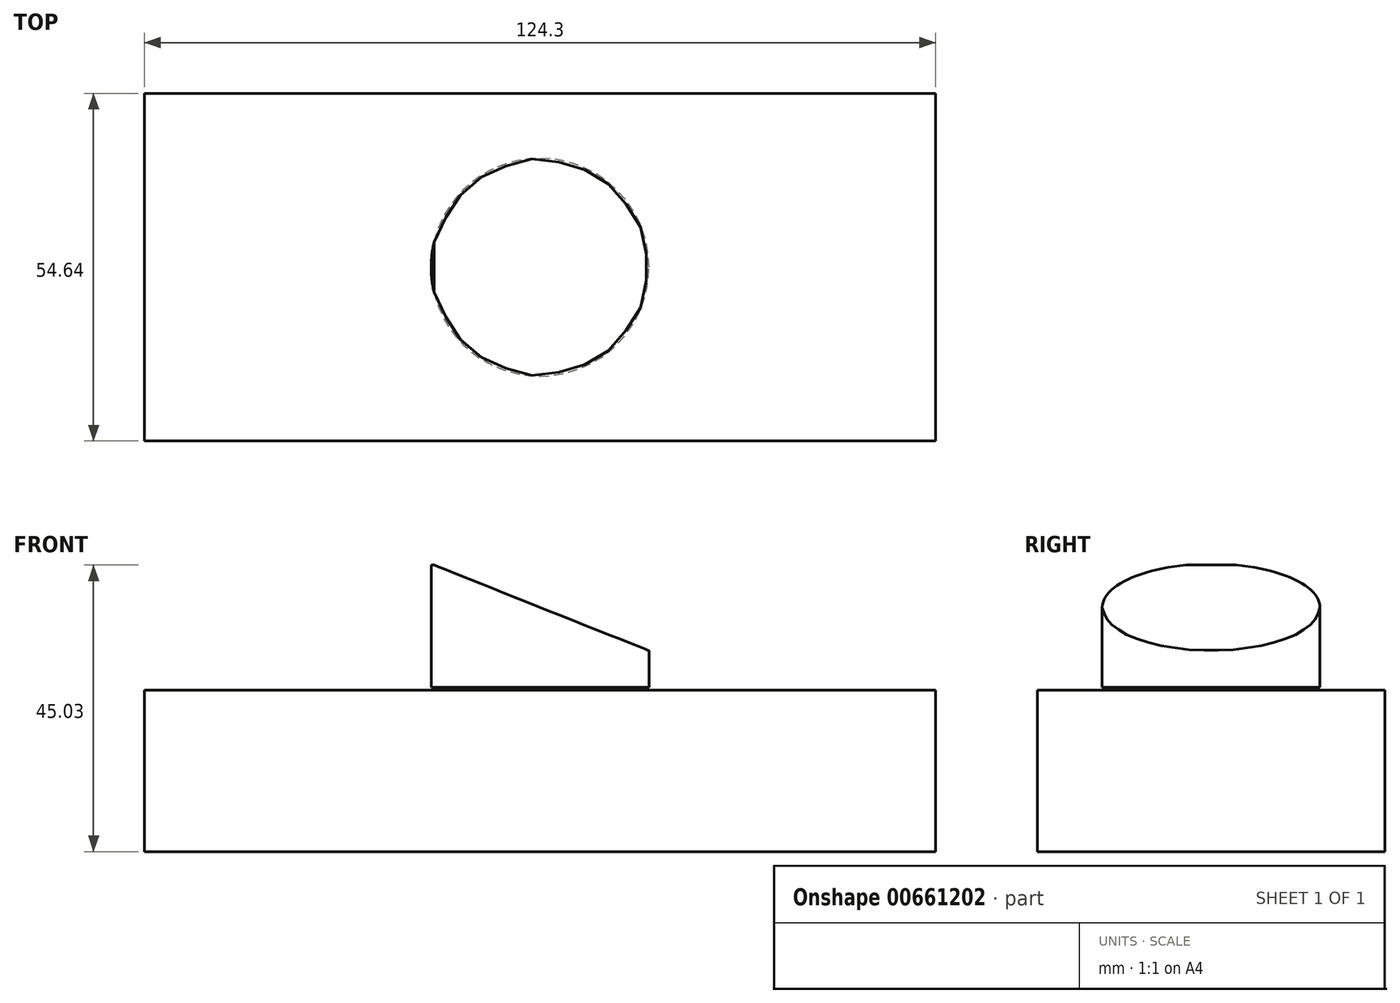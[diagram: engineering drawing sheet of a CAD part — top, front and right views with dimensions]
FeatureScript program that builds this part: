
annotation { "Feature Type Name" : "Feature", "Feature Type Description" : "" }
export const myFeature = defineFeature(function(context is Context, id is Id, definition is map)
    precondition{}
    {
        {
            var Q0;
            Q0=qCreatedBy(makeId("Top.planeOp"),FACE);
            var sketch = newSketch(context, id + "F0", { "sketchPlane" : qUnion([Q0])});
            skLineSegment(sketch, "E0.bottom", {"start": v(-62.15, 27.32) * mm, "end": v(62.15, 27.32) * mm});
            skLineSegment(sketch, "E0.top", {"start": v(-62.15, -27.32) * mm, "end": v(62.15, -27.32) * mm});
            skLineSegment(sketch, "E0.left", {"start": v(-62.15, 27.32) * mm, "end": v(-62.15, -27.32) * mm});
            skLineSegment(sketch, "E0.right", {"start": v(62.15, 27.32) * mm, "end": v(62.15, -27.32) * mm});
            skPoint(sketch, "E0.middle", {"position": v(0, 0) * mm});
            skSolve(sketch);
        }
        {
            var Q0;
            Q0 = qSketchRegion(id + "F0", true);
            extrude(context, id + "F1", {"entities" : qUnion([Q0]), "depth" : 25.4 * mm, "offsetDistance" : 25.4 * mm});
        }
        {
            var Q0;
            Q0=qCreatedBy(makeId("Front.planeOp"),FACE);
            var sketch = newSketch(context, id + "F2", { "sketchPlane" : qUnion([Q0])});
            skLineSegment(sketch, "E1.bottom", {"start": v(0, 25.82) * mm, "end": v(-17.11, 25.82) * mm});
            skLineSegment(sketch, "E1.top", {"start": v(0, 45.03) * mm, "end": v(-17.11, 45.03) * mm});
            skLineSegment(sketch, "E1.left", {"start": v(0, 25.82) * mm, "end": v(0, 45.03) * mm});
            skLineSegment(sketch, "E1.right", {"start": v(-17.11, 25.82) * mm, "end": v(-17.11, 45.03) * mm});
            skSolve(sketch);
        }
        {
            var Q0;
            Q0=makeQuery(id+"F2.imprint","IMPRINT",FACE,{"disambiguationData":[TD([[makeQuery(id+"F2.imprint","IMPRINT",EDGE,{"derivedFrom":sQuery(id+"F2.wireOp",EDGE,"E1.bottom")}),-1.0]])]});
            var Q1;
            Q1=sQuery(id+"F2.wireOp",EDGE,"E1.left");
            revolve(context, id + "F3", {"entities" : qUnion([Q0]), "axis" : qUnion([Q1]), "revolveType" : RevolveType.FULL});
        }
        {
            var Q0;
            Q0=qCreatedBy(makeId("Front.planeOp"),FACE);
            var sketch = newSketch(context, id + "F4", { "sketchPlane" : qUnion([Q0])});
            skLineSegment(sketch, "E2", {"start": v(-18.91, 45.93) * mm, "end": v(23.82, 28.91) * mm});
            skLineSegment(sketch, "E3", {"start": v(23.82, 28.91) * mm, "end": v(36.58, 60.96) * mm});
            skLineSegment(sketch, "E4", {"start": v(36.58, 60.96) * mm, "end": v(-6.15, 77.98) * mm});
            skLineSegment(sketch, "E5", {"start": v(-6.15, 77.98) * mm, "end": v(-18.91, 45.93) * mm});
            skSolve(sketch);
        }
        {
            var Q0;
            Q0=makeQuery(id+"F4.imprint","IMPRINT",FACE,{"disambiguationData":[TD([[makeQuery(id+"F4.imprint","IMPRINT",EDGE,{"derivedFrom":sQuery(id+"F4.wireOp",EDGE,"E2")}),1.0]])]});
            var Q1;
            Q1=sQuery(id+"F4.wireOp",EDGE,"E5");
            revolve(context, id + "F5", {"operationType" : NewBodyOperationType.REMOVE, "entities" : qUnion([Q0]), "axis" : qUnion([Q1]), "revolveType" : RevolveType.FULL, "oppositeDirection" : true});
        }
    });
